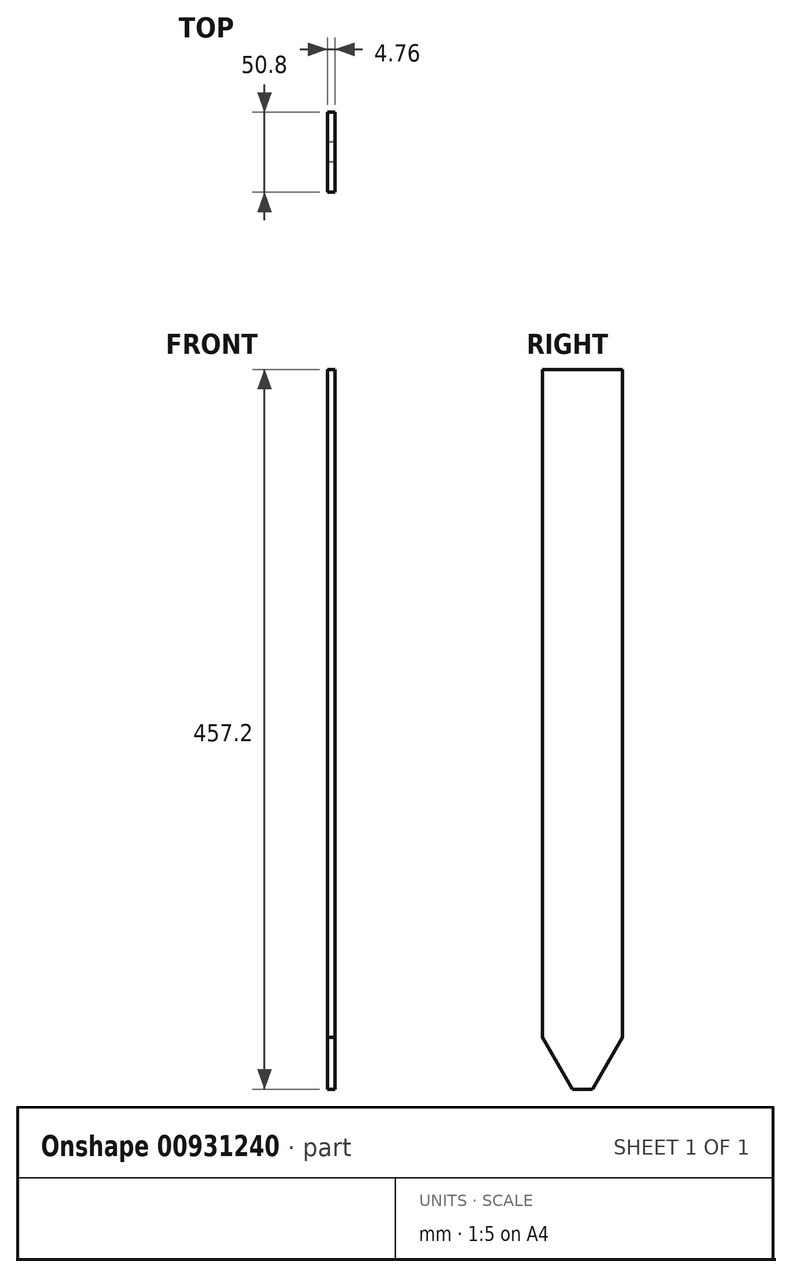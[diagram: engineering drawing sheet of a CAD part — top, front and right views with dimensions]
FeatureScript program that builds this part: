
annotation { "Feature Type Name" : "Feature", "Feature Type Description" : "" }
export const myFeature = defineFeature(function(context is Context, id is Id, definition is map)
    precondition{}
    {
        {
            var Q0;
            Q0=qCreatedBy(makeId("Right.planeOp"),FACE);
            var sketch = newSketch(context, id + "F0", { "sketchPlane" : qUnion([Q0])});
            skLineSegment(sketch, "E0.bottom", {"start": v(0, 0) * mm, "end": v(50.8, 0) * mm});
            skLineSegment(sketch, "E0.top", {"start": v(0, 457.2) * mm, "end": v(50.8, 457.2) * mm});
            skLineSegment(sketch, "E0.left", {"start": v(0, 0) * mm, "end": v(0, 457.2) * mm});
            skLineSegment(sketch, "E0.right", {"start": v(50.8, 0) * mm, "end": v(50.8, 457.2) * mm});
            skLineSegment(sketch, "E1", {"start": v(31.75, 0) * mm, "end": v(50.8, 33) * mm});
            skLineSegment(sketch, "E2", {"start": v(19.05, 0) * mm, "end": v(0, 33) * mm});
            skSolve(sketch);
        }
        {
            var Q0;
            {var subQ1=sQuery(id+"F0.wireOp",EDGE,"E0.top");Q0=makeQuery(id+"F0.imprint","IMPRINT",FACE,{"disambiguationData":[TD([[makeQuery(id+"F0.imprint","IMPRINT",EDGE,{"derivedFrom":subQ1}),-1.0]])]});}
            extrude(context, id + "F1", {"entities" : qUnion([Q0]), "depth" : 4.76 * mm, "offsetDistance" : 25.4 * mm});
        }
    });
